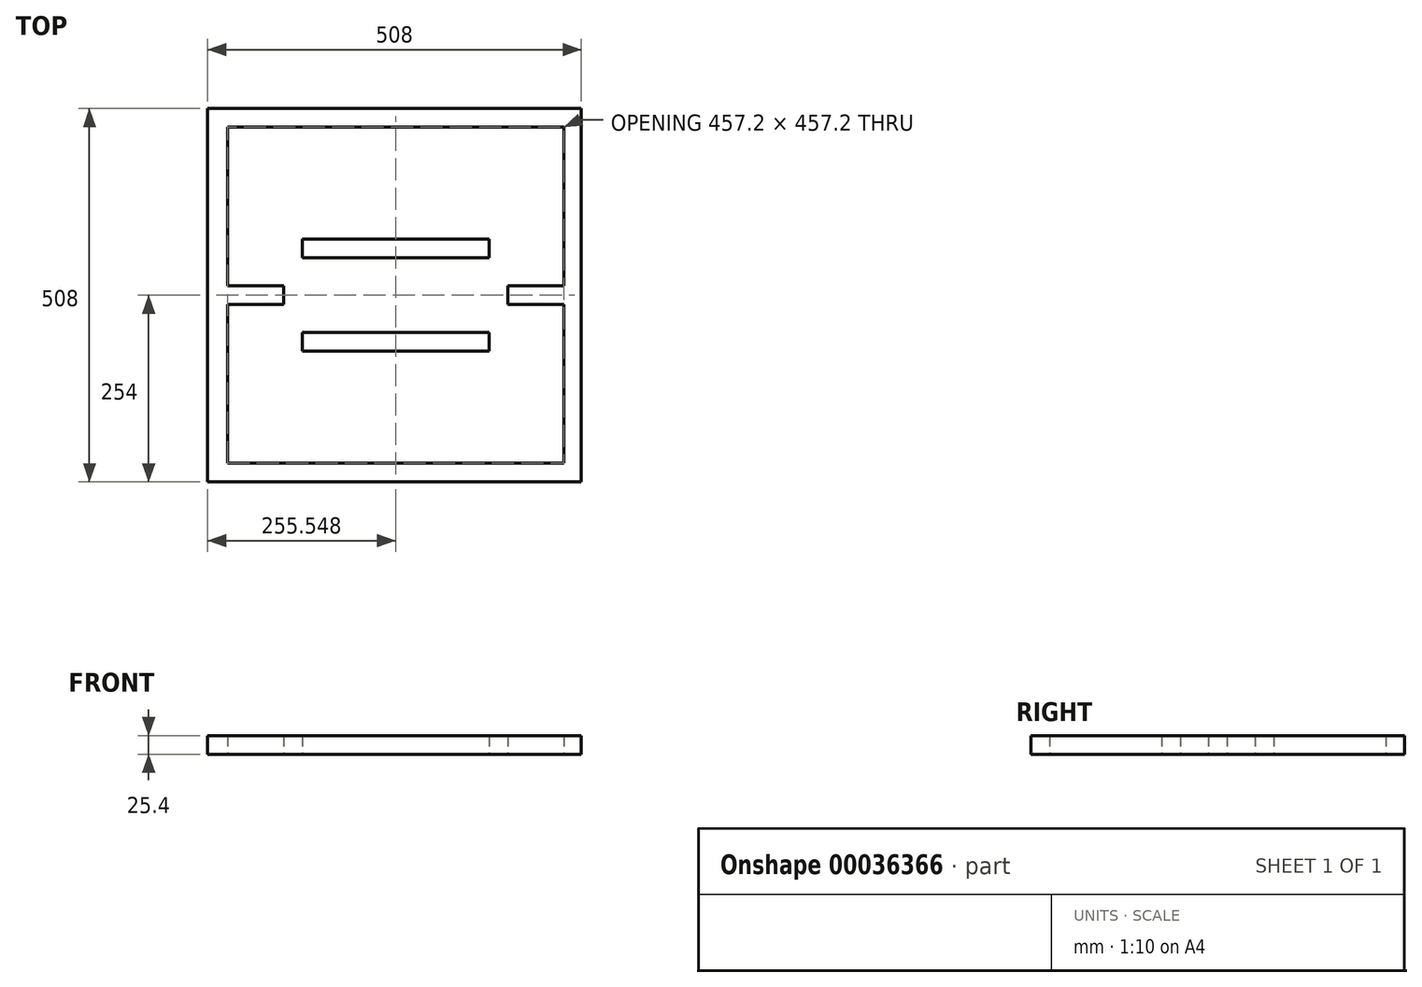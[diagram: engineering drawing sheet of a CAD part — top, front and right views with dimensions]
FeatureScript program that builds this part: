
annotation { "Feature Type Name" : "Feature", "Feature Type Description" : "" }
export const myFeature = defineFeature(function(context is Context, id is Id, definition is map)
    precondition{}
    {
        {
            var Q0;
            Q0=qCreatedBy(makeId("Top.planeOp"),FACE);
            var sketch = newSketch(context, id + "F0", { "sketchPlane" : qUnion([Q0])});
            skLineSegment(sketch, "E0.bottom", {"start": v(-392, 304.8) * mm, "end": v(116, 304.8) * mm});
            skLineSegment(sketch, "E0.top", {"start": v(-392, -203.2) * mm, "end": v(116, -203.2) * mm});
            skLineSegment(sketch, "E0.left", {"start": v(-392, 304.8) * mm, "end": v(-392, -203.2) * mm});
            skLineSegment(sketch, "E0.right", {"start": v(116, 304.8) * mm, "end": v(116, -203.2) * mm});
            skLineSegment(sketch, "E1.bottom", {"start": v(-365.05, 279.4) * mm, "end": v(92.15, 279.4) * mm});
            skLineSegment(sketch, "E1.top", {"start": v(-365.05, -177.8) * mm, "end": v(92.15, -177.8) * mm});
            skLineSegment(sketch, "E1.left", {"start": v(-365.05, 279.4) * mm, "end": v(-365.05, -177.8) * mm});
            skLineSegment(sketch, "E1.right", {"start": v(92.15, 279.4) * mm, "end": v(92.15, -177.8) * mm});
            skLineSegment(sketch, "E2.bottom", {"start": v(15.95, 279.4) * mm, "end": v(-9.45, 279.4) * mm});
            skLineSegment(sketch, "E2.top", {"start": v(15.95, -177.8) * mm, "end": v(-9.45, -177.8) * mm});
            skLineSegment(sketch, "E2.left", {"start": v(15.95, 279.4) * mm, "end": v(15.95, -177.8) * mm});
            skLineSegment(sketch, "E2.right", {"start": v(-9.45, 279.4) * mm, "end": v(-9.45, -177.8) * mm});
            skLineSegment(sketch, "E3.bottom", {"start": v(-263.45, -177.8) * mm, "end": v(-288.85, -177.8) * mm});
            skLineSegment(sketch, "E3.top", {"start": v(-263.45, 279.4) * mm, "end": v(-288.85, 279.4) * mm});
            skLineSegment(sketch, "E3.left", {"start": v(-263.45, -177.8) * mm, "end": v(-263.45, 279.4) * mm});
            skLineSegment(sketch, "E3.right", {"start": v(-288.85, -177.8) * mm, "end": v(-288.85, 279.4) * mm});
            skLineSegment(sketch, "E4.bottom", {"start": v(-9.45, 127) * mm, "end": v(-263.45, 127) * mm});
            skLineSegment(sketch, "E4.top", {"start": v(-9.45, 101.6) * mm, "end": v(-263.45, 101.6) * mm});
            skLineSegment(sketch, "E4.left", {"start": v(-9.45, 127) * mm, "end": v(-9.45, 101.6) * mm});
            skLineSegment(sketch, "E4.right", {"start": v(-263.45, 127) * mm, "end": v(-263.45, 101.6) * mm});
            skLineSegment(sketch, "E5.bottom", {"start": v(-263.45, 0) * mm, "end": v(-9.45, 0) * mm});
            skLineSegment(sketch, "E5.top", {"start": v(-263.45, -25.4) * mm, "end": v(-9.45, -25.4) * mm});
            skLineSegment(sketch, "E5.left", {"start": v(-263.45, 0) * mm, "end": v(-263.45, -25.4) * mm});
            skLineSegment(sketch, "E5.right", {"start": v(-9.45, 0) * mm, "end": v(-9.45, -25.4) * mm});
            skLineSegment(sketch, "E6.bottom", {"start": v(-288.85, 63.5) * mm, "end": v(-365.05, 63.5) * mm});
            skLineSegment(sketch, "E6.top", {"start": v(-288.85, 38.1) * mm, "end": v(-365.05, 38.1) * mm});
            skLineSegment(sketch, "E6.left", {"start": v(-288.85, 63.5) * mm, "end": v(-288.85, 38.1) * mm});
            skLineSegment(sketch, "E6.right", {"start": v(-365.05, 63.5) * mm, "end": v(-365.05, 38.1) * mm});
            skLineSegment(sketch, "E7.bottom", {"start": v(15.95, 63.5) * mm, "end": v(92.15, 63.5) * mm});
            skLineSegment(sketch, "E7.top", {"start": v(15.95, 38.1) * mm, "end": v(92.15, 38.1) * mm});
            skLineSegment(sketch, "E7.left", {"start": v(15.95, 63.5) * mm, "end": v(15.95, 38.1) * mm});
            skLineSegment(sketch, "E7.right", {"start": v(92.15, 63.5) * mm, "end": v(92.15, 38.1) * mm});
            skSolve(sketch);
        }
        {
            var Q0;
            Q0=makeQuery(id+"F0.imprint","IMPRINT",FACE,{"disambiguationData":[TD([[makeQuery(id+"F0.imprint","IMPRINT",EDGE,{"derivedFrom":sQuery(id+"F0.wireOp",EDGE,"E0.bottom")}),-1.0]])]});
            var Q1;
            {var subQ7=sQuery(id+"F0.wireOp",EDGE,"E2.bottom");Q1=makeQuery(id+"F0.imprint","IMPRINT",FACE,{"disambiguationData":[TD([[makeQuery(id+"F0.imprint","IMPRINT",EDGE,{"derivedFrom":subQ7}),1.0]])]});}
            var Q2;
            Q2=makeQuery(id+"F0.imprint","IMPRINT",FACE,{"disambiguationData":[TD([[makeQuery(id+"F0.imprint","IMPRINT",EDGE,{"derivedFrom":sQuery(id+"F0.wireOp",EDGE,"E4.bottom")}),1.0]])]});
            var Q3;
            Q3=makeQuery(id+"F0.imprint","IMPRINT",FACE,{"disambiguationData":[TD([[makeQuery(id+"F0.imprint","IMPRINT",EDGE,{"derivedFrom":sQuery(id+"F0.wireOp",EDGE,"E5.bottom")}),-1.0]])]});
            var Q4;
            Q4=makeQuery(id+"F0.imprint","IMPRINT",FACE,{"disambiguationData":[TD([[makeQuery(id+"F0.imprint","IMPRINT",EDGE,{"derivedFrom":sQuery(id+"F0.wireOp",EDGE,"E7.bottom")}),-1.0]])]});
            var Q5;
            Q5=makeQuery(id+"F0.imprint","IMPRINT",FACE,{"disambiguationData":[TD([[makeQuery(id+"F0.imprint","IMPRINT",EDGE,{"derivedFrom":sQuery(id+"F0.wireOp",EDGE,"E6.bottom")}),1.0]])]});
            var Q6;
            {var subQ7=sQuery(id+"F0.wireOp",EDGE,"E3.bottom");Q6=makeQuery(id+"F0.imprint","IMPRINT",FACE,{"disambiguationData":[TD([[makeQuery(id+"F0.imprint","IMPRINT",EDGE,{"derivedFrom":subQ7}),-1.0]])]});}
            extrude(context, id + "F1", {"entities" : qUnion([Q0, Q1, Q2, Q3, Q4, Q5, Q6]), "depth" : 25.4 * mm});
        }
    });
